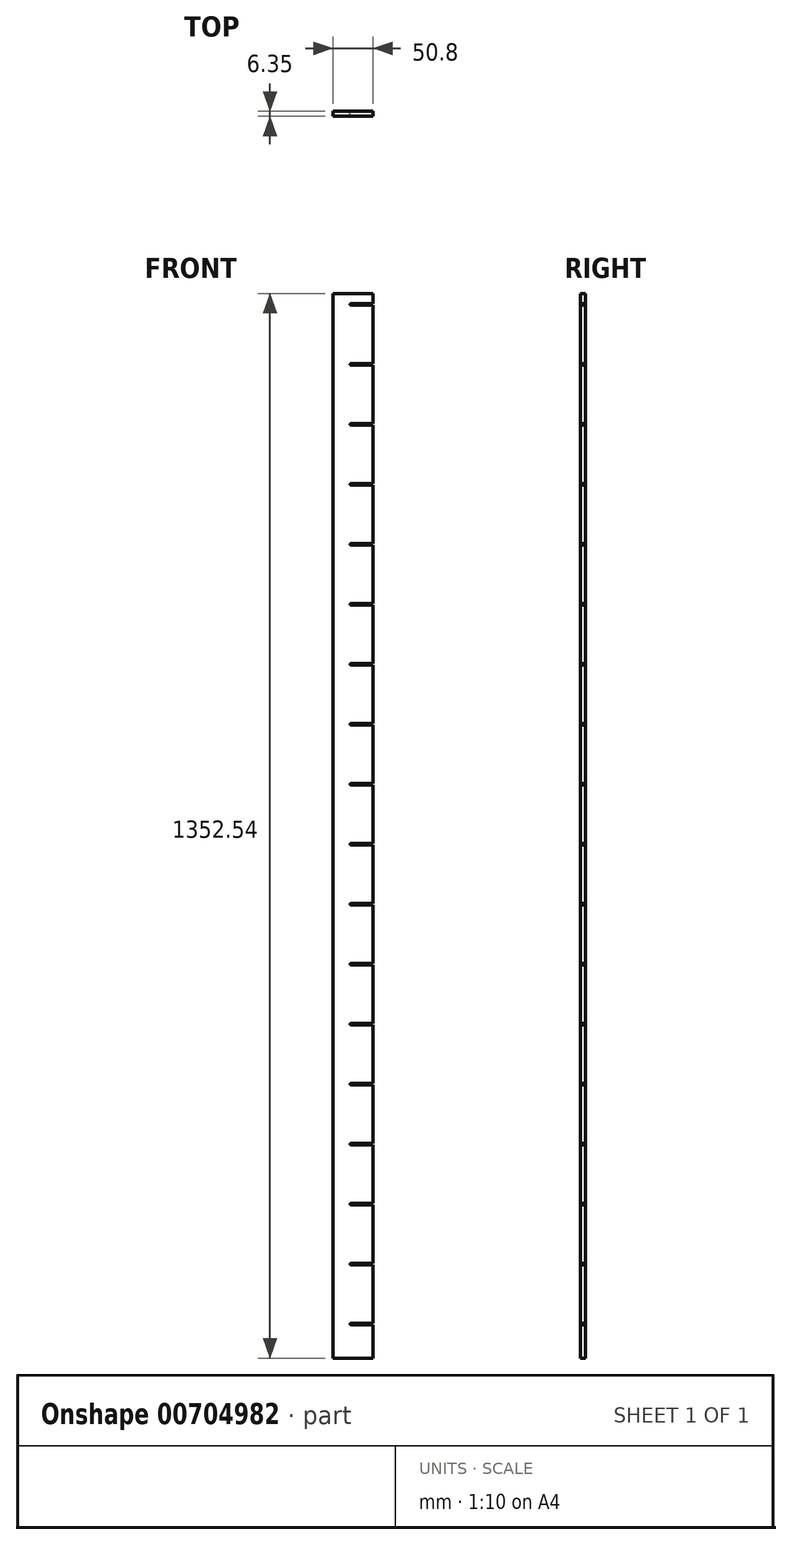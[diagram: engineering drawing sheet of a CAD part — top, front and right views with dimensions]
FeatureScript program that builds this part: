
annotation { "Feature Type Name" : "Feature", "Feature Type Description" : "" }
export const myFeature = defineFeature(function(context is Context, id is Id, definition is map)
    precondition{}
    {
        {
            var Q0;
            Q0=qCreatedBy(makeId("Front.planeOp"),FACE);
            var sketch = newSketch(context, id + "F0", { "sketchPlane" : qUnion([Q0])});
            skLineSegment(sketch, "E0.bottom", {"start": v(25.4, -676.28) * mm, "end": v(-25.4, -676.28) * mm});
            skLineSegment(sketch, "E0.top", {"start": v(25.4, 676.28) * mm, "end": v(-25.4, 676.28) * mm});
            skLineSegment(sketch, "E0.left", {"start": v(25.4, -676.28) * mm, "end": v(25.4, -633.86) * mm});
            skLineSegment(sketch, "E0.right", {"start": v(-25.4, -676.28) * mm, "end": v(-25.4, 676.28) * mm});
            skPoint(sketch, "E0.middle", {"position": v(0, 0) * mm});
            skLineSegment(sketch, "E1.trimOffspring", {"start": v(25.4, 663.58) * mm, "end": v(25.4, 676.28) * mm});
            skArc(sketch, "E2.1.0.2", {"start": v(-2.54, 663.58) * mm, "mid": v(-3.56, 662.56) * mm, "end": v(-2.54, 661.54) * mm});
            skLineSegment(sketch, "E2.direction1", {"start": v(-2.54, 663.58) * mm, "end": v(-2.54, 663.58) * mm});
            skLineSegment(sketch, "E2.direction2", {"start": v(-2.54, 663.58) * mm, "end": v(-2.54, 661.54) * mm, "construction": true});
            skLineSegment(sketch, "E3.trimOffspring", {"start": v(25.4, 587.38) * mm, "end": v(25.4, 661.54) * mm});
            skLineSegment(sketch, "E4.trimOffspring", {"start": v(25.4, 511.18) * mm, "end": v(25.4, 585.34) * mm});
            skLineSegment(sketch, "E5.trimOffspring", {"start": v(25.4, 358.78) * mm, "end": v(25.4, 509.14) * mm});
            skLineSegment(sketch, "E6.trimOffspring", {"start": v(25.4, 282.58) * mm, "end": v(25.4, 356.74) * mm});
            skLineSegment(sketch, "E7.trimOffspring", {"start": v(25.4, 206.38) * mm, "end": v(25.4, 280.54) * mm});
            skLineSegment(sketch, "E8.trimOffspring", {"start": v(25.4, 130.18) * mm, "end": v(25.4, 204.34) * mm});
            skLineSegment(sketch, "E9.trimOffspring", {"start": v(25.4, 53.98) * mm, "end": v(25.4, 128.14) * mm});
            skLineSegment(sketch, "E10.trimOffspring", {"start": v(25.4, -22.22) * mm, "end": v(25.4, 51.94) * mm});
            skLineSegment(sketch, "E11.trimOffspring", {"start": v(25.4, -98.42) * mm, "end": v(25.4, -24.26) * mm});
            skLineSegment(sketch, "E12.trimOffspring", {"start": v(25.4, -174.62) * mm, "end": v(25.4, -100.46) * mm});
            skLineSegment(sketch, "E13.trimOffspring", {"start": v(25.4, -250.82) * mm, "end": v(25.4, -176.66) * mm});
            skLineSegment(sketch, "E14.trimOffspring", {"start": v(25.4, -327.02) * mm, "end": v(25.4, -252.86) * mm});
            skLineSegment(sketch, "E15.trimOffspring", {"start": v(25.4, -403.22) * mm, "end": v(25.4, -329.06) * mm});
            skLineSegment(sketch, "E16.trimOffspring", {"start": v(25.4, -479.42) * mm, "end": v(25.4, -405.26) * mm});
            skLineSegment(sketch, "E17.trimOffspring", {"start": v(25.4, -555.62) * mm, "end": v(25.4, -481.46) * mm});
            skLineSegment(sketch, "E18.trimOffspring", {"start": v(25.4, -631.82) * mm, "end": v(25.4, -557.66) * mm});
            skPoint(sketch, "E2.1.0.0.end.orphan", {"position": v(25.4, 663.58) * mm});
            skLineSegment(sketch, "E19", {"start": v(-2.54, 663.58) * mm, "end": v(25.4, 663.58) * mm});
            skLineSegment(sketch, "E20", {"start": v(-2.54, 661.54) * mm, "end": v(25.4, 661.54) * mm});
            skPoint(sketch, "E2.2.0.2.start.orphan", {"position": v(-2.54, 663.58) * mm});
            skLineSegment(sketch, "E21.0.1.0", {"start": v(-2.54, 585.34) * mm, "end": v(25.4, 585.34) * mm});
            skArc(sketch, "E21.0.1.1", {"start": v(-2.54, 587.38) * mm, "mid": v(-3.56, 586.36) * mm, "end": v(-2.54, 585.34) * mm});
            skLineSegment(sketch, "E21.0.1.2", {"start": v(-2.54, 587.38) * mm, "end": v(25.4, 587.38) * mm});
            skLineSegment(sketch, "E21.0.2.0", {"start": v(-2.54, 509.14) * mm, "end": v(25.4, 509.14) * mm});
            skArc(sketch, "E21.0.2.1", {"start": v(-2.54, 511.17) * mm, "mid": v(-3.56, 510.16) * mm, "end": v(-2.54, 509.14) * mm});
            skLineSegment(sketch, "E21.0.2.2", {"start": v(-2.54, 511.17) * mm, "end": v(25.4, 511.17) * mm});
            skLineSegment(sketch, "E21.0.3.0", {"start": v(-2.54, 432.94) * mm, "end": v(25.4, 432.94) * mm});
            skArc(sketch, "E21.0.3.1", {"start": v(-2.54, 434.97) * mm, "mid": v(-3.56, 433.96) * mm, "end": v(-2.54, 432.94) * mm});
            skLineSegment(sketch, "E21.0.3.2", {"start": v(-2.54, 434.97) * mm, "end": v(25.4, 434.97) * mm});
            skLineSegment(sketch, "E21.0.4.0", {"start": v(-2.54, 356.74) * mm, "end": v(25.4, 356.74) * mm});
            skArc(sketch, "E21.0.4.1", {"start": v(-2.54, 358.77) * mm, "mid": v(-3.56, 357.76) * mm, "end": v(-2.54, 356.74) * mm});
            skLineSegment(sketch, "E21.0.4.2", {"start": v(-2.54, 358.77) * mm, "end": v(25.4, 358.77) * mm});
            skLineSegment(sketch, "E21.0.5.0", {"start": v(-2.54, 280.54) * mm, "end": v(25.4, 280.54) * mm});
            skArc(sketch, "E21.0.5.1", {"start": v(-2.54, 282.57) * mm, "mid": v(-3.56, 281.56) * mm, "end": v(-2.54, 280.54) * mm});
            skLineSegment(sketch, "E21.0.5.2", {"start": v(-2.54, 282.57) * mm, "end": v(25.4, 282.57) * mm});
            skLineSegment(sketch, "E21.0.6.0", {"start": v(-2.54, 204.34) * mm, "end": v(25.4, 204.34) * mm});
            skArc(sketch, "E21.0.6.1", {"start": v(-2.54, 206.37) * mm, "mid": v(-3.56, 205.36) * mm, "end": v(-2.54, 204.34) * mm});
            skLineSegment(sketch, "E21.0.6.2", {"start": v(-2.54, 206.37) * mm, "end": v(25.4, 206.37) * mm});
            skLineSegment(sketch, "E21.0.7.0", {"start": v(-2.54, 128.14) * mm, "end": v(25.4, 128.14) * mm});
            skArc(sketch, "E21.0.7.1", {"start": v(-2.54, 130.17) * mm, "mid": v(-3.56, 129.16) * mm, "end": v(-2.54, 128.14) * mm});
            skLineSegment(sketch, "E21.0.7.2", {"start": v(-2.54, 130.17) * mm, "end": v(25.4, 130.17) * mm});
            skLineSegment(sketch, "E21.0.8.0", {"start": v(-2.54, 51.94) * mm, "end": v(25.4, 51.94) * mm});
            skArc(sketch, "E21.0.8.1", {"start": v(-2.54, 53.97) * mm, "mid": v(-3.56, 52.96) * mm, "end": v(-2.54, 51.94) * mm});
            skLineSegment(sketch, "E21.0.8.2", {"start": v(-2.54, 53.97) * mm, "end": v(25.4, 53.97) * mm});
            skLineSegment(sketch, "E21.0.9.0", {"start": v(-2.54, -24.26) * mm, "end": v(25.4, -24.26) * mm});
            skArc(sketch, "E21.0.9.1", {"start": v(-2.54, -22.23) * mm, "mid": v(-3.56, -23.24) * mm, "end": v(-2.54, -24.26) * mm});
            skLineSegment(sketch, "E21.0.9.2", {"start": v(-2.54, -22.23) * mm, "end": v(25.4, -22.23) * mm});
            skLineSegment(sketch, "E21.0.10.0", {"start": v(-2.54, -100.46) * mm, "end": v(25.4, -100.46) * mm});
            skArc(sketch, "E21.0.10.1", {"start": v(-2.54, -98.43) * mm, "mid": v(-3.56, -99.44) * mm, "end": v(-2.54, -100.46) * mm});
            skLineSegment(sketch, "E21.0.10.2", {"start": v(-2.54, -98.43) * mm, "end": v(25.4, -98.43) * mm});
            skLineSegment(sketch, "E21.0.11.0", {"start": v(-2.54, -176.66) * mm, "end": v(25.4, -176.66) * mm});
            skArc(sketch, "E21.0.11.1", {"start": v(-2.54, -174.63) * mm, "mid": v(-3.56, -175.64) * mm, "end": v(-2.54, -176.66) * mm});
            skLineSegment(sketch, "E21.0.11.2", {"start": v(-2.54, -174.63) * mm, "end": v(25.4, -174.63) * mm});
            skLineSegment(sketch, "E21.0.12.0", {"start": v(-2.54, -252.86) * mm, "end": v(25.4, -252.86) * mm});
            skArc(sketch, "E21.0.12.1", {"start": v(-2.54, -250.83) * mm, "mid": v(-3.56, -251.84) * mm, "end": v(-2.54, -252.86) * mm});
            skLineSegment(sketch, "E21.0.12.2", {"start": v(-2.54, -250.83) * mm, "end": v(25.4, -250.83) * mm});
            skLineSegment(sketch, "E21.0.13.0", {"start": v(-2.54, -329.06) * mm, "end": v(25.4, -329.06) * mm});
            skArc(sketch, "E21.0.13.1", {"start": v(-2.54, -327.03) * mm, "mid": v(-3.56, -328.04) * mm, "end": v(-2.54, -329.06) * mm});
            skLineSegment(sketch, "E21.0.13.2", {"start": v(-2.54, -327.03) * mm, "end": v(25.4, -327.03) * mm});
            skLineSegment(sketch, "E21.0.14.0", {"start": v(-2.54, -405.26) * mm, "end": v(25.4, -405.26) * mm});
            skArc(sketch, "E21.0.14.1", {"start": v(-2.54, -403.23) * mm, "mid": v(-3.56, -404.24) * mm, "end": v(-2.54, -405.26) * mm});
            skLineSegment(sketch, "E21.0.14.2", {"start": v(-2.54, -403.23) * mm, "end": v(25.4, -403.23) * mm});
            skLineSegment(sketch, "E21.0.15.0", {"start": v(-2.54, -481.46) * mm, "end": v(25.4, -481.46) * mm});
            skArc(sketch, "E21.0.15.1", {"start": v(-2.54, -479.43) * mm, "mid": v(-3.56, -480.44) * mm, "end": v(-2.54, -481.46) * mm});
            skLineSegment(sketch, "E21.0.15.2", {"start": v(-2.54, -479.43) * mm, "end": v(25.4, -479.43) * mm});
            skLineSegment(sketch, "E21.0.16.0", {"start": v(-2.54, -557.66) * mm, "end": v(25.4, -557.66) * mm});
            skArc(sketch, "E21.0.16.1", {"start": v(-2.54, -555.63) * mm, "mid": v(-3.56, -556.64) * mm, "end": v(-2.54, -557.66) * mm});
            skLineSegment(sketch, "E21.0.16.2", {"start": v(-2.54, -555.63) * mm, "end": v(25.4, -555.63) * mm});
            skLineSegment(sketch, "E21.0.17.0", {"start": v(-2.54, -633.86) * mm, "end": v(25.4, -633.86) * mm});
            skArc(sketch, "E21.0.17.1", {"start": v(-2.54, -631.83) * mm, "mid": v(-3.56, -632.84) * mm, "end": v(-2.54, -633.86) * mm});
            skLineSegment(sketch, "E21.0.17.2", {"start": v(-2.54, -631.83) * mm, "end": v(25.4, -631.83) * mm});
            skLineSegment(sketch, "E21.direction2", {"start": v(-2.54, 661.54) * mm, "end": v(-2.54, 585.34) * mm, "construction": true});
            skSolve(sketch);
        }
        {
            var Q0;
            Q0=makeQuery(id+"F0.imprint","IMPRINT",FACE,{"disambiguationData":[TD([[makeQuery(id+"F0.imprint","IMPRINT",EDGE,{"derivedFrom":sQuery(id+"F0.wireOp",EDGE,"E0.bottom")}),-1.0]])]});
            extrude(context, id + "F1", {"entities" : qUnion([Q0]), "depth" : 6.35 * mm, "offsetDistance" : 25.4 * mm});
        }
    });
